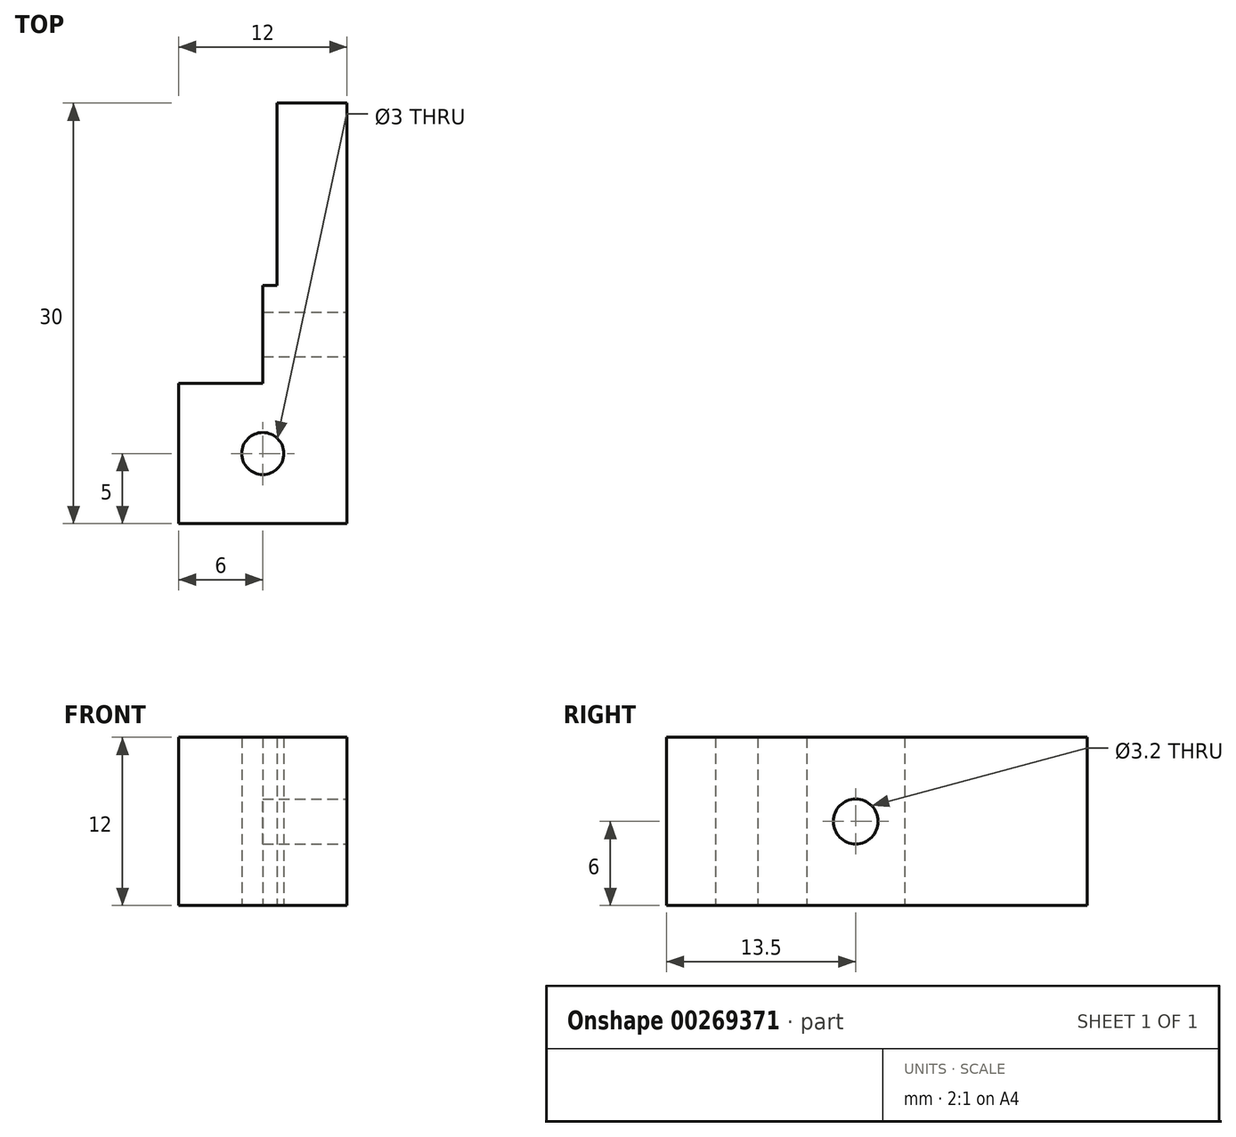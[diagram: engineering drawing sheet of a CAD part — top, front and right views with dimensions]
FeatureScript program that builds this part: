
annotation { "Feature Type Name" : "Feature", "Feature Type Description" : "" }
export const myFeature = defineFeature(function(context is Context, id is Id, definition is map)
    precondition{}
    {
        {
            var Q0;
            Q0=qCreatedBy(makeId("Top.planeOp"),FACE);
            var sketch = newSketch(context, id + "F0", { "sketchPlane" : qUnion([Q0])});
            skLineSegment(sketch, "E0.bottom", {"start": v(6, 20) * mm, "end": v(1, 20) * mm});
            skLineSegment(sketch, "E0.top", {"start": v(6, -10) * mm, "end": v(-6, -10) * mm});
            skLineSegment(sketch, "E0.left", {"start": v(6, 20) * mm, "end": v(6, -10) * mm});
            skLineSegment(sketch, "E0.right", {"start": v(-6, 0) * mm, "end": v(-6, -10) * mm});
            skPoint(sketch, "E0.middle", {"position": v(0, 0) * mm});
            skLineSegment(sketch, "E1", {"start": v(0, 7) * mm, "end": v(0, 0) * mm});
            skLineSegment(sketch, "E2", {"start": v(-6, 0) * mm, "end": v(0, 0) * mm});
            skCircle(sketch, "E3", {"center": v(0, -5) * mm, "radius": 1.5 * mm});
            skLineSegment(sketch, "E4", {"start": v(0, 7) * mm, "end": v(1, 7) * mm});
            skLineSegment(sketch, "E5", {"start": v(1, 7) * mm, "end": v(1, 20) * mm});
            skSolve(sketch);
        }
        {
            var Q0;
            Q0=makeQuery(id+"F0.imprint","IMPRINT",FACE,{"disambiguationData":[TD([[makeQuery(id+"F0.imprint","IMPRINT",EDGE,{"derivedFrom":sQuery(id+"F0.wireOp",EDGE,"E0.bottom")}),1.0]])]});
            extrude(context, id + "F1", {"entities" : qUnion([Q0]), "endBound" : BoundingType.SYMMETRIC, "depth" : 12 * mm});
        }
        {
            var Q0;
            Q0=makeQuery(id+"F1.opExtrude","SWEPT_FACE",FACE,{"disambiguationData":[OSD([sQuery(id+"F0.wireOp",EDGE,"E0.left")])]});
            cPlane(context, id + "F2", {"entities" : qUnion([Q0]), "cplaneType" : CPlaneType.OFFSET, "offset" : 0 * mm, "width" : 150 * mm, "height" : 150 * mm});
        }
        {
            var Q0;
            Q0=qCreatedBy(id+"F2.planeOp",FACE);
            var sketch = newSketch(context, id + "F3", { "sketchPlane" : qUnion([Q0])});
            skLineSegment(sketch, "E6", {"start": v(0, 0) * mm, "end": v(3.5, 0) * mm});
            skCircle(sketch, "E7", {"center": v(3.5, 0) * mm, "radius": 1.6 * mm});
            skSolve(sketch);
        }
        {
            var Q0;
            Q0=makeQuery(id+"F3.imprint","IMPRINT",FACE,{"disambiguationData":[TD([[makeQuery(id+"F3.imprint","IMPRINT",EDGE,{"derivedFrom":sQuery(id+"F3.wireOp",EDGE,"E7")}),1.0]])]});
            var Q1;
            Q1=sQuery(id+"F3.wireOp",EDGE,"E7");
            extrude(context, id + "F4", {"entities" : qUnion([Q0]), "operationType" : NewBodyOperationType.REMOVE, "surfaceEntities" : qUnion([Q1]), "oppositeDirection" : true, "depth" : 25 * mm});
        }
    });
